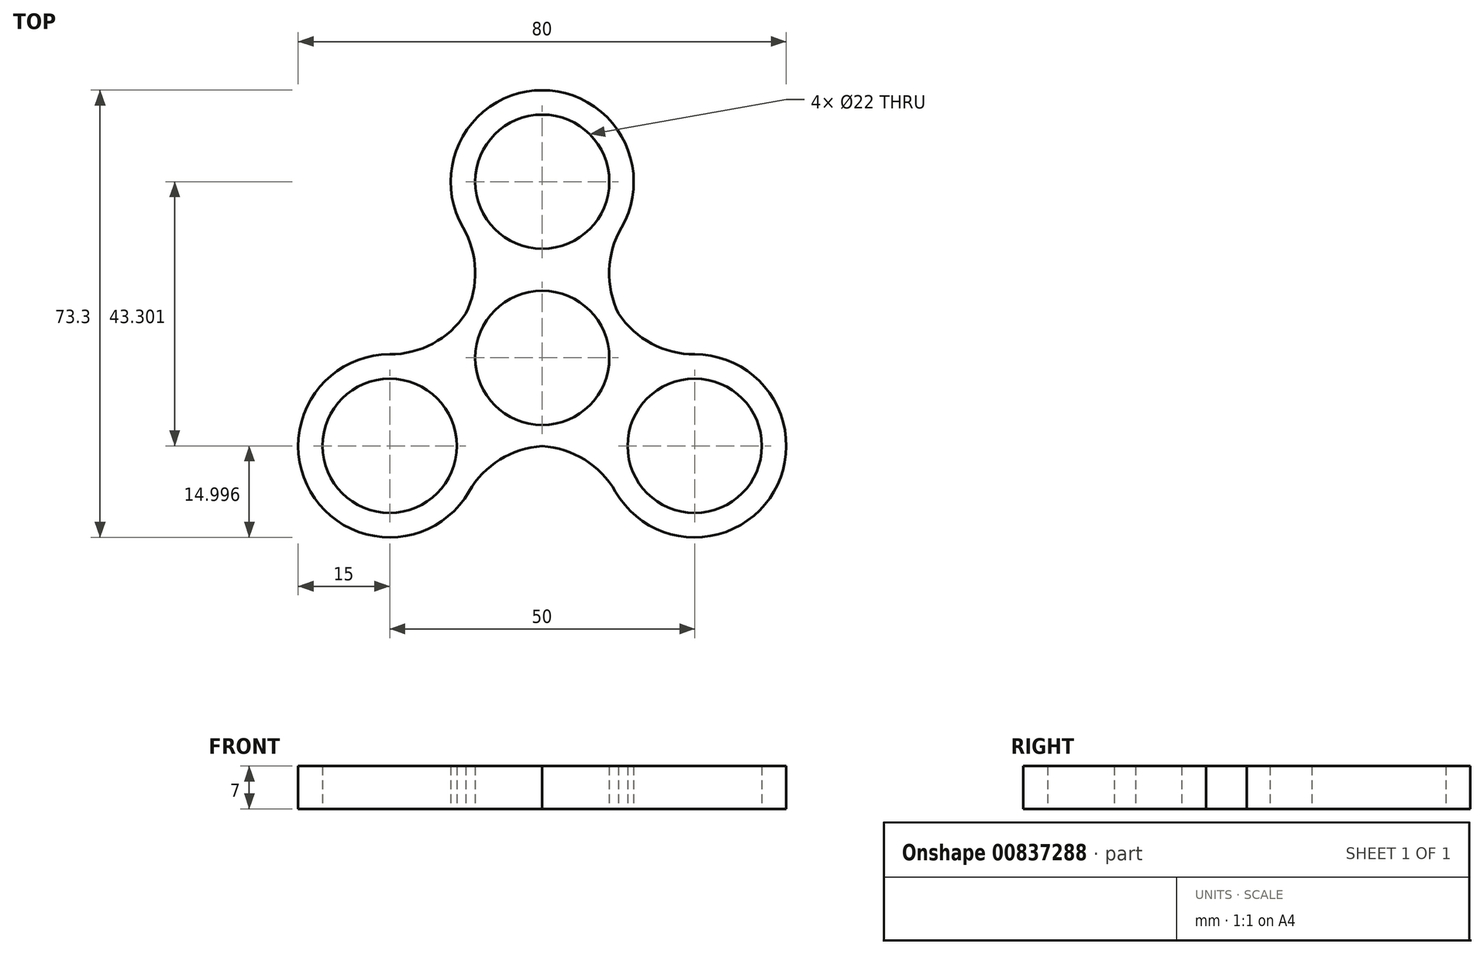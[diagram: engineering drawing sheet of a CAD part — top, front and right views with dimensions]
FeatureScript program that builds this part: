
annotation { "Feature Type Name" : "Feature", "Feature Type Description" : "" }
export const myFeature = defineFeature(function(context is Context, id is Id, definition is map)
    precondition{}
    {
        {
            var Q0;
            Q0=qCreatedBy(makeId("Top.planeOp"),FACE);
            var sketch = newSketch(context, id + "F0", { "sketchPlane" : qUnion([Q0])});
            skCircle(sketch, "E0.cCircle", {"center": v(0, 0) * mm, "radius": 14.43 * mm, "construction": true});
            skLineSegment(sketch, "E0.0", {"start": v(25, -14.43) * mm, "end": v(-25, -14.43) * mm});
            skLineSegment(sketch, "E0.1", {"start": v(-25, -14.43) * mm, "end": v(0, 28.87) * mm});
            skLineSegment(sketch, "E0.2", {"start": v(0, 28.87) * mm, "end": v(25, -14.43) * mm});
            skPoint(sketch, "E0.0.midPoint", {"position": v(0, -14.43) * mm});
            skCircle(sketch, "E1", {"center": v(0, 28.87) * mm, "radius": 15 * mm});
            skCircle(sketch, "E2", {"center": v(25, -14.43) * mm, "radius": 15 * mm});
            skCircle(sketch, "E3", {"center": v(-25, -14.43) * mm, "radius": 15 * mm});
            skCircle(sketch, "E4", {"center": v(0, 28.87) * mm, "radius": 11 * mm});
            skCircle(sketch, "E5", {"center": v(0, 0) * mm, "radius": 11 * mm});
            skCircle(sketch, "E6", {"center": v(25, -14.43) * mm, "radius": 11 * mm});
            skCircle(sketch, "E7", {"center": v(-25, -14.43) * mm, "radius": 11 * mm});
            skSolve(sketch);
        }
        {
            var Q0;
            Q0 = qSketchRegion(id + "F0", true);
            extrude(context, id + "F1", {"entities" : qUnion([Q0]), "depth" : 7 * mm, "offsetDistance" : 25 * mm});
        }
        {
            var Q0;
            Q0=makeQuery(id+"F1.opExtrude","SWEPT_EDGE",EDGE,{"disambiguationData":[OSD([sQuery(id+"F0.wireOp",EDGE,"E0.2"),sQuery(id+"F0.wireOp",EDGE,"E1")])]});
            var Q1;
            Q1=makeQuery(id+"F1.opExtrude","SWEPT_EDGE",EDGE,{"disambiguationData":[OSD([sQuery(id+"F0.wireOp",EDGE,"E0.2"),sQuery(id+"F0.wireOp",EDGE,"E2")])]});
            var Q2;
            Q2=makeQuery(id+"F1.opExtrude","SWEPT_EDGE",EDGE,{"disambiguationData":[OSD([sQuery(id+"F0.wireOp",EDGE,"E0.1"),sQuery(id+"F0.wireOp",EDGE,"E1")])]});
            var Q3;
            Q3=makeQuery(id+"F1.opExtrude","SWEPT_EDGE",EDGE,{"disambiguationData":[OSD([sQuery(id+"F0.wireOp",EDGE,"E0.1"),sQuery(id+"F0.wireOp",EDGE,"E3")])]});
            var Q4;
            Q4=makeQuery(id+"F1.opExtrude","SWEPT_EDGE",EDGE,{"disambiguationData":[OSD([sQuery(id+"F0.wireOp",EDGE,"E0.0"),sQuery(id+"F0.wireOp",EDGE,"E3")])]});
            var Q5;
            Q5=makeQuery(id+"F1.opExtrude","SWEPT_EDGE",EDGE,{"disambiguationData":[OSD([sQuery(id+"F0.wireOp",EDGE,"E0.0"),sQuery(id+"F0.wireOp",EDGE,"E2")])]});
            fillet(context, id + "F2", {"entities" : qUnion([Q0, Q1, Q2, Q3, Q4, Q5]), "radius" : 15 * mm, "tangentPropagation" : true, "allowEdgeOverflow" : false});
        }
    });
